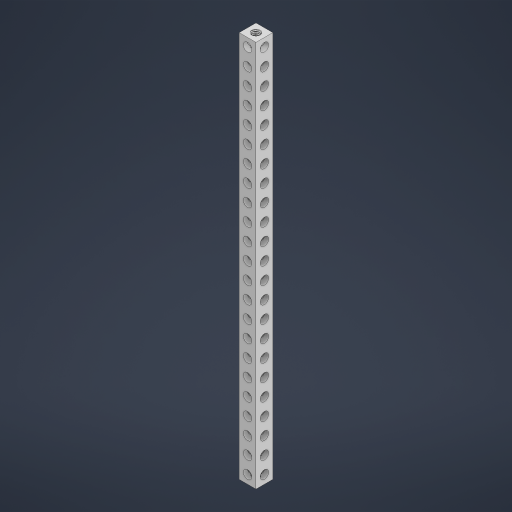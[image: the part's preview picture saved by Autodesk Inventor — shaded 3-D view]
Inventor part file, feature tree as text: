
AUTODESK INVENTOR PART (.ipt)
format: ipt  version: 2023 (Build 270158000, 158)  size: 1,250,816 bytes
history: native  units: in
note: dims shown in document units (in); Inventor stores cm internally (conversion verified against a paired STEP export)
features: mirror x1
ambient origin geometry x8: Origin, YZ Plane, XZ Plane, XY Plane, X Axis, Y Axis, Z Axis, Center Point
bodies: Solid1 (feature_tree)
feature tree (1):
  mirror  "Mirror3"
